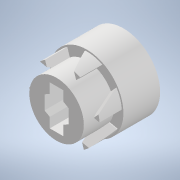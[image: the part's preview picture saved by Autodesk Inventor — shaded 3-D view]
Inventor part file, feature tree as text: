
AUTODESK INVENTOR PART (.ipt)
format: ipt  version: 2022 (Build 260153000, 153)  size: 289,792 bytes
history: native  units: mm
features: other x5, sketch x4, extrude x4, reference x4, projected_geometry x4, plane x3, chamfer x1, pattern_circular x1
ambient origin geometry x8: Origin, YZ Plane, XZ Plane, XY Plane, X Axis, Y Axis, Z Axis, Center Point
bodies: Solid1 (feature_tree)
feature tree (26):
  sketch  "Sketch1"  dims[d1=0.5mm d2=10.0mm d3=0.0mm]
  plane  "Work Plane1"
  extrude  "Extrusion1"  Depth=10.0mm TaperAngle=0.0deg
  sketch  "Sketch2"  dims[d4=0.3mm d5=10.0mm d6=0.0mm d7=2.6mm d8=2.0mm d9=11.34464mm]
  plane  "Work Plane2"
  extrude  "Extrusion2"  Depth=10.0mm TaperAngle=0.0deg
  chamfer  "Chamfer1"  Distance=2.6mm
  extrude  "Extrusion3"  Depth=1.5mm TaperAngle=360.0deg
  pattern_circular  "Circular Pattern1"  [2 undecoded]
  sketch  "Sketch4"  dims[d15=0.2mm d17=10.0mm d18=0.0mm d19=0.3mm]
  plane  "Work Plane3"
  extrude  "Extrusion4"  Depth=10.0mm
  reference  "Reference1"
  reference  "Reference2"
  reference  "Reference3"
  projected_geometry  "Projected Loop1"
  sketch  "Sketch3"  dims[d10=1.5mm d11=0.0mm d12=60.0mm d13=360.0deg]
  projected_geometry  "Projected Loop2"
  reference  "Reference4"
  projected_geometry  "Projected Loop3"
  projected_geometry  "Projected Loop4"
  other  "<userpath>\OneDrive - Imperial College London\ROBOICP\Final Assembly\Final Assembly.iam"
  other  "Final Assembly.iam"
  other  "new top 4.0:1"
  other  "male head_1.75R:1"
  other  "Mixer:1"
note: 2 required parameter values undecoded (feature->parameter linkage not recoverable at this tier; creation-order binding heuristic only, values carry confidence <= 0.55)
